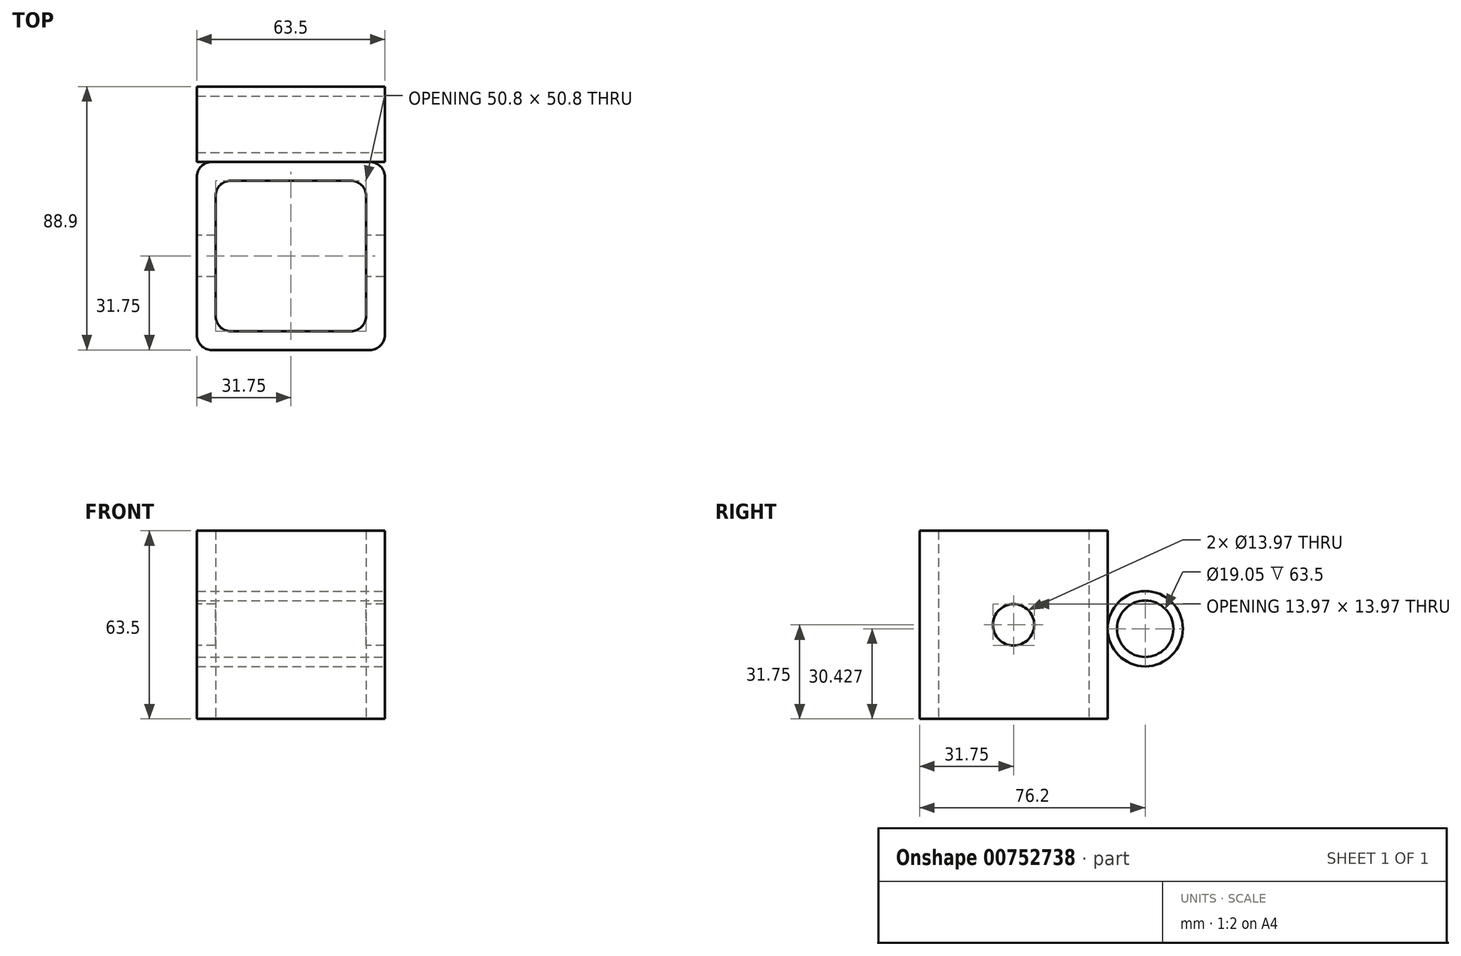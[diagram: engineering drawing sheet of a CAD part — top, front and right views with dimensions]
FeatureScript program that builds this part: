
annotation { "Feature Type Name" : "Feature", "Feature Type Description" : "" }
export const myFeature = defineFeature(function(context is Context, id is Id, definition is map)
    precondition{}
    {
        {
            var Q0;
            Q0=qCreatedBy(makeId("Top.planeOp"),FACE);
            var sketch = newSketch(context, id + "F0", { "sketchPlane" : qUnion([Q0])});
            skLineSegment(sketch, "E0.bottom", {"start": v(31.75, 31.75) * mm, "end": v(-31.75, 31.75) * mm});
            skLineSegment(sketch, "E0.top", {"start": v(31.75, -31.75) * mm, "end": v(-31.75, -31.75) * mm});
            skLineSegment(sketch, "E0.left", {"start": v(31.75, 31.75) * mm, "end": v(31.75, -31.75) * mm});
            skLineSegment(sketch, "E0.right", {"start": v(-31.75, 31.75) * mm, "end": v(-31.75, -31.75) * mm});
            skPoint(sketch, "E0.middle", {"position": v(0, 0) * mm});
            skLineSegment(sketch, "E1.bottom", {"start": v(25.4, 25.4) * mm, "end": v(-25.4, 25.4) * mm});
            skLineSegment(sketch, "E1.top", {"start": v(25.4, -25.4) * mm, "end": v(-25.4, -25.4) * mm});
            skLineSegment(sketch, "E1.left", {"start": v(25.4, 25.4) * mm, "end": v(25.4, -25.4) * mm});
            skLineSegment(sketch, "E1.right", {"start": v(-25.4, 25.4) * mm, "end": v(-25.4, -25.4) * mm});
            skSolve(sketch);
        }
        {
            var Q0;
            Q0 = qSketchRegion(id + "F0", true);
            extrude(context, id + "F1", {"entities" : qUnion([Q0]), "depth" : 63.5 * mm, "offsetDistance" : 25.4 * mm});
        }
        {
            var Q0;
            Q0=makeQuery(id+"F1.opExtrude","SWEPT_EDGE",EDGE,{"disambiguationData":[OSD([sQuery(id+"F0.wireOp",EDGE,"E0.top"),sQuery(id+"F0.wireOp",EDGE,"E0.left")])]});
            var Q1;
            Q1=makeQuery(id+"F1.opExtrude","SWEPT_EDGE",EDGE,{"disambiguationData":[OSD([sQuery(id+"F0.wireOp",EDGE,"E0.top"),sQuery(id+"F0.wireOp",EDGE,"E0.right")])]});
            var Q2;
            Q2=makeQuery(id+"F1.opExtrude","SWEPT_EDGE",EDGE,{"disambiguationData":[OSD([sQuery(id+"F0.wireOp",EDGE,"E0.bottom"),sQuery(id+"F0.wireOp",EDGE,"E0.right")])]});
            var Q3;
            Q3=makeQuery(id+"F1.opExtrude","SWEPT_EDGE",EDGE,{"disambiguationData":[OSD([sQuery(id+"F0.wireOp",EDGE,"E0.bottom"),sQuery(id+"F0.wireOp",EDGE,"E0.left")])]});
            var Q4;
            Q4=makeQuery(id+"F1.opExtrude","SWEPT_EDGE",EDGE,{"disambiguationData":[OSD([sQuery(id+"F0.wireOp",EDGE,"E1.top"),sQuery(id+"F0.wireOp",EDGE,"E1.left")])]});
            var Q5;
            Q5=makeQuery(id+"F1.opExtrude","SWEPT_EDGE",EDGE,{"disambiguationData":[OSD([sQuery(id+"F0.wireOp",EDGE,"E1.bottom"),sQuery(id+"F0.wireOp",EDGE,"E1.left")])]});
            var Q6;
            Q6=makeQuery(id+"F1.opExtrude","SWEPT_EDGE",EDGE,{"disambiguationData":[OSD([sQuery(id+"F0.wireOp",EDGE,"E1.bottom"),sQuery(id+"F0.wireOp",EDGE,"E1.right")])]});
            var Q7;
            Q7=makeQuery(id+"F1.opExtrude","SWEPT_EDGE",EDGE,{"disambiguationData":[OSD([sQuery(id+"F0.wireOp",EDGE,"E1.top"),sQuery(id+"F0.wireOp",EDGE,"E1.right")])]});
            fillet(context, id + "F2", {"entities" : qUnion([Q0, Q1, Q2, Q3, Q4, Q5, Q6, Q7]), "radius" : 5.08 * mm, "tangentPropagation" : true, "allowEdgeOverflow" : false});
        }
        {
            var Q0;
            Q0=makeQuery(id+"F1.opExtrude","SWEPT_FACE",FACE,{"disambiguationData":[OSD([sQuery(id+"F0.wireOp",EDGE,"E0.right")])]});
            var sketch = newSketch(context, id + "F3", { "sketchPlane" : qUnion([Q0])});
            skCircle(sketch, "E2", {"center": v(0, 31.75) * mm, "radius": 6.99 * mm});
            skSolve(sketch);
        }
        {
            var Q0;
            Q0 = qSketchRegion(id + "F3", true);
            extrude(context, id + "F4", {"entities" : qUnion([Q0]), "operationType" : NewBodyOperationType.REMOVE, "oppositeDirection" : true, "depth" : 63.5 * mm, "offsetDistance" : 25.4 * mm});
        }
        {
            var Q0;
            Q0=makeQuery(id+"F1.opExtrude","SWEPT_FACE",FACE,{"disambiguationData":[OSD([sQuery(id+"F0.wireOp",EDGE,"E0.left")])]});
            var sketch = newSketch(context, id + "F5", { "sketchPlane" : qUnion([Q0])});
            skCircle(sketch, "E3", {"center": v(44.45, 30.43) * mm, "radius": 12.7 * mm});
            skCircle(sketch, "E4", {"center": v(44.45, 30.43) * mm, "radius": 9.53 * mm});
            skSolve(sketch);
        }
        {
            var Q0;
            Q0 = qSketchRegion(id + "F5", true);
            extrude(context, id + "F6", {"entities" : qUnion([Q0]), "operationType" : NewBodyOperationType.ADD, "oppositeDirection" : true, "depth" : 63.5 * mm, "offsetDistance" : 25.4 * mm});
        }
    });
